# Revit family: Specialty_Equipment-Fiberglass_Planter-Planters_Unlimited-Imperial Urn GFRC
name_source: partatom
category: Specialty Equipment
units: mm (PartAtom-declared; Revit-internal decimal feet)

## family parameters
Always vertical = Yes
Cut with Voids When Loaded = No
Enable Cutting in Views = No
Maintain Annotation Orientation = No
OmniClass Number = 23.40.05.21.17
OmniClass Title = Planters
Part Type = Normal
Room Calculation Point = No
Round Connector Dimension = Use Diameter
Shared = No
Work Plane-Based = No

## types (1)
- 30"Dia x 36"H
    Assembly Code = G2050600
    CD_Diameter = 30.0"
    CD_Finish = Concrete-Fiberstone-Carlsbad-Chenza
    CD_Height = 36.0"
    CD_Microsite = https://www.caddetails.com
    CD_Product Page URL = https://www.plantersunlimited.com
    CD_Specification = https://www.plantersunlimited.com
    Default Elevation = 0.0"
    Description = Imperial Urn Planter
    Manufacturer = Planters Unlimited
    Model = Imperial Series Planter
    Type Comments = Imperial Planter
    URL = https://www.plantersunlimited.com

## geometry (parser evidence)
native form markers: Sweep x3
no freeform markers — native parametric forms only
